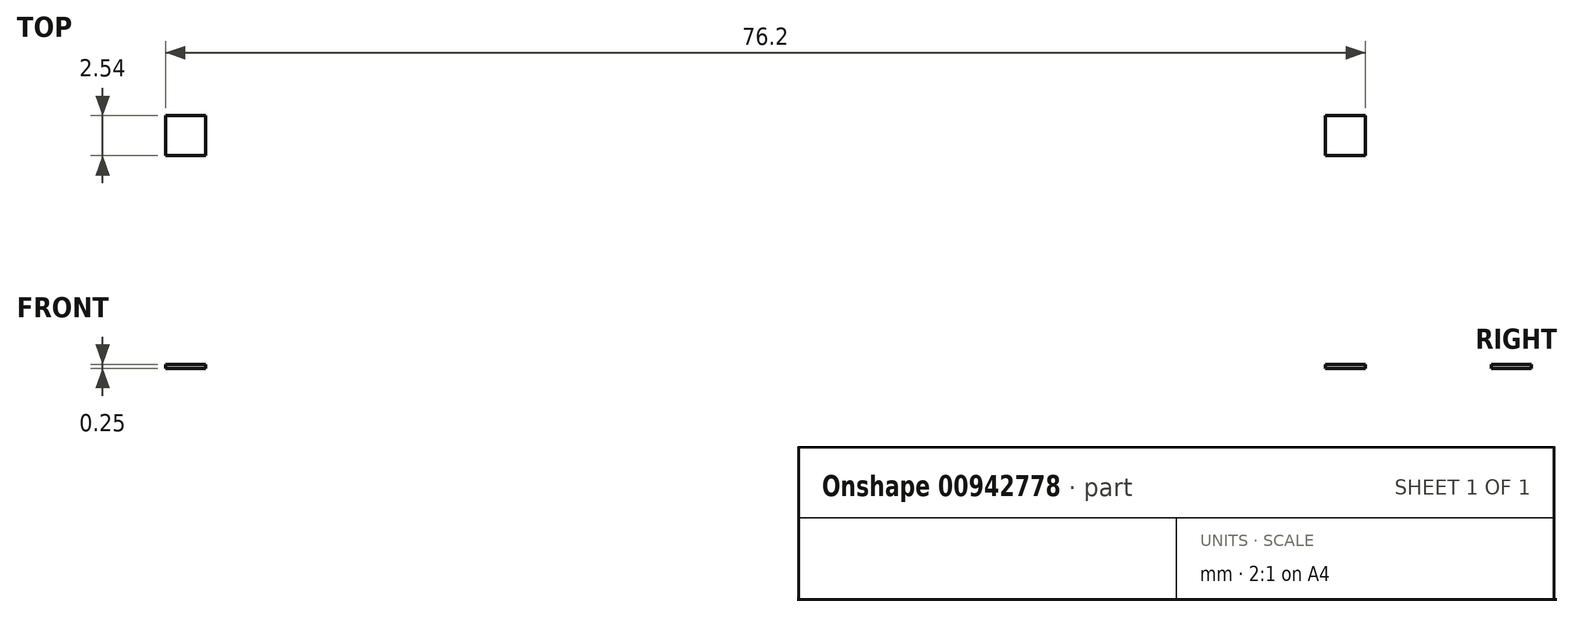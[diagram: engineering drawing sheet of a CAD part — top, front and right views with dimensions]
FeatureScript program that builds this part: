
annotation { "Feature Type Name" : "Feature", "Feature Type Description" : "" }
export const myFeature = defineFeature(function(context is Context, id is Id, definition is map)
    precondition{}
    {
        {
            var Q0;
            Q0=qCreatedBy(makeId("Top.planeOp"),FACE);
            var sketch = newSketch(context, id + "F0", { "sketchPlane" : qUnion([Q0])});
            skLineSegment(sketch, "E0.bottom", {"start": v(0, 0) * mm, "end": v(76.2, 0) * mm});
            skLineSegment(sketch, "E0.top", {"start": v(0, 59.18) * mm, "end": v(76.2, 59.18) * mm});
            skLineSegment(sketch, "E0.left", {"start": v(0, 0) * mm, "end": v(0, 59.18) * mm});
            skLineSegment(sketch, "E0.right", {"start": v(76.2, 0) * mm, "end": v(76.2, 59.18) * mm});
            skLineSegment(sketch, "E1.bottom", {"start": v(0, 59.18) * mm, "end": v(2.54, 59.18) * mm});
            skLineSegment(sketch, "E1.top", {"start": v(0, 56.64) * mm, "end": v(2.54, 56.64) * mm});
            skLineSegment(sketch, "E1.left", {"start": v(0, 59.18) * mm, "end": v(0, 56.64) * mm});
            skLineSegment(sketch, "E1.right", {"start": v(2.54, 59.18) * mm, "end": v(2.54, 56.64) * mm});
            skLineSegment(sketch, "E2.bottom", {"start": v(76.2, 59.18) * mm, "end": v(73.66, 59.18) * mm});
            skLineSegment(sketch, "E2.top", {"start": v(76.2, 56.64) * mm, "end": v(73.66, 56.64) * mm});
            skLineSegment(sketch, "E2.left", {"start": v(76.2, 59.18) * mm, "end": v(76.2, 56.64) * mm});
            skLineSegment(sketch, "E2.right", {"start": v(73.66, 59.18) * mm, "end": v(73.66, 56.64) * mm});
            skLineSegment(sketch, "E3.bottom", {"start": v(76.2, 0) * mm, "end": v(73.66, 0) * mm});
            skLineSegment(sketch, "E3.top", {"start": v(76.2, 2.54) * mm, "end": v(73.66, 2.54) * mm});
            skLineSegment(sketch, "E3.left", {"start": v(76.2, 0) * mm, "end": v(76.2, 2.54) * mm});
            skLineSegment(sketch, "E3.right", {"start": v(73.66, 0) * mm, "end": v(73.66, 2.54) * mm});
            skLineSegment(sketch, "E4.bottom", {"start": v(0, 0) * mm, "end": v(2.54, 0) * mm});
            skLineSegment(sketch, "E4.top", {"start": v(0, 2.54) * mm, "end": v(2.54, 2.54) * mm});
            skLineSegment(sketch, "E4.left", {"start": v(0, 0) * mm, "end": v(0, 2.54) * mm});
            skLineSegment(sketch, "E4.right", {"start": v(2.54, 0) * mm, "end": v(2.54, 2.54) * mm});
            skLineSegment(sketch, "E5", {"start": v(1.27, 2.54) * mm, "end": v(1.27, 6.75) * mm});
            skLineSegment(sketch, "E6", {"start": v(1.27, 2.54) * mm, "end": v(1.27, 4.65) * mm});
            skLineSegment(sketch, "E7", {"start": v(2.54, 1.27) * mm, "end": v(6.68, 1.27) * mm});
            skLineSegment(sketch, "E8", {"start": v(6.68, 1.27) * mm, "end": v(4.6, 1.27) * mm});
            skLineSegment(sketch, "E9", {"start": v(2.54, 57.91) * mm, "end": v(6.75, 57.91) * mm});
            skLineSegment(sketch, "E10", {"start": v(6.75, 57.91) * mm, "end": v(4.64, 57.91) * mm});
            skLineSegment(sketch, "E11", {"start": v(1.27, 56.64) * mm, "end": v(1.27, 52.42) * mm});
            skLineSegment(sketch, "E12", {"start": v(1.27, 52.42) * mm, "end": v(1.27, 54.53) * mm});
            skLineSegment(sketch, "E13", {"start": v(73.66, 57.91) * mm, "end": v(69.44, 57.91) * mm});
            skLineSegment(sketch, "E14", {"start": v(69.44, 57.91) * mm, "end": v(71.55, 57.91) * mm});
            skLineSegment(sketch, "E15", {"start": v(74.93, 56.64) * mm, "end": v(74.93, 52.43) * mm});
            skLineSegment(sketch, "E16", {"start": v(74.93, 52.43) * mm, "end": v(74.93, 54.54) * mm});
            skLineSegment(sketch, "E17", {"start": v(74.93, 2.54) * mm, "end": v(74.93, 6.76) * mm});
            skLineSegment(sketch, "E18", {"start": v(74.93, 6.76) * mm, "end": v(74.93, 4.65) * mm});
            skLineSegment(sketch, "E19", {"start": v(73.66, 1.27) * mm, "end": v(69.44, 1.27) * mm});
            skLineSegment(sketch, "E20", {"start": v(69.44, 1.27) * mm, "end": v(71.55, 1.27) * mm});
            skCircle(sketch, "E21", {"center": v(71.55, 1.27) * mm, "radius": 0.5 * mm});
            skCircle(sketch, "E22", {"center": v(69.44, 1.27) * mm, "radius": 0.52 * mm});
            skCircle(sketch, "E23", {"center": v(74.93, 4.65) * mm, "radius": 0.52 * mm});
            skCircle(sketch, "E24", {"center": v(74.93, 6.76) * mm, "radius": 0.5 * mm});
            skCircle(sketch, "E25", {"center": v(69.44, 57.91) * mm, "radius": 0.52 * mm});
            skCircle(sketch, "E26", {"center": v(71.55, 57.91) * mm, "radius": 0.5 * mm});
            skCircle(sketch, "E27", {"center": v(74.93, 54.54) * mm, "radius": 0.52 * mm});
            skCircle(sketch, "E28", {"center": v(74.93, 52.43) * mm, "radius": 0.5 * mm});
            skCircle(sketch, "E29", {"center": v(6.75, 57.91) * mm, "radius": 0.51 * mm});
            skCircle(sketch, "E30", {"center": v(4.64, 57.91) * mm, "radius": 0.51 * mm});
            skCircle(sketch, "E31", {"center": v(1.27, 54.53) * mm, "radius": 0.5 * mm});
            skCircle(sketch, "E32", {"center": v(1.27, 52.42) * mm, "radius": 0.5 * mm});
            skCircle(sketch, "E33", {"center": v(1.27, 6.75) * mm, "radius": 0.5 * mm});
            skCircle(sketch, "E34", {"center": v(1.27, 4.65) * mm, "radius": 0.5 * mm});
            skCircle(sketch, "E35", {"center": v(4.6, 1.27) * mm, "radius": 0.51 * mm});
            skCircle(sketch, "E36", {"center": v(6.68, 1.27) * mm, "radius": 0.5 * mm});
            skSolve(sketch);
        }
        {
            var Q0;
            {var subQ11=sQuery(id+"F0.wireOp",EDGE,"E0.bottom");Q0=makeQuery(id+"F0.imprint","IMPRINT",FACE,{"disambiguationData":[TD([[makeQuery(id+"F0.imprint","IMPRINT",EDGE,{"derivedFrom":subQ11}),1.0]])]});}
            extrude(context, id + "F1", {"entities" : qUnion([Q0]), "depth" : 0.25 * mm, "offsetDistance" : 25.4 * mm});
        }
    });
